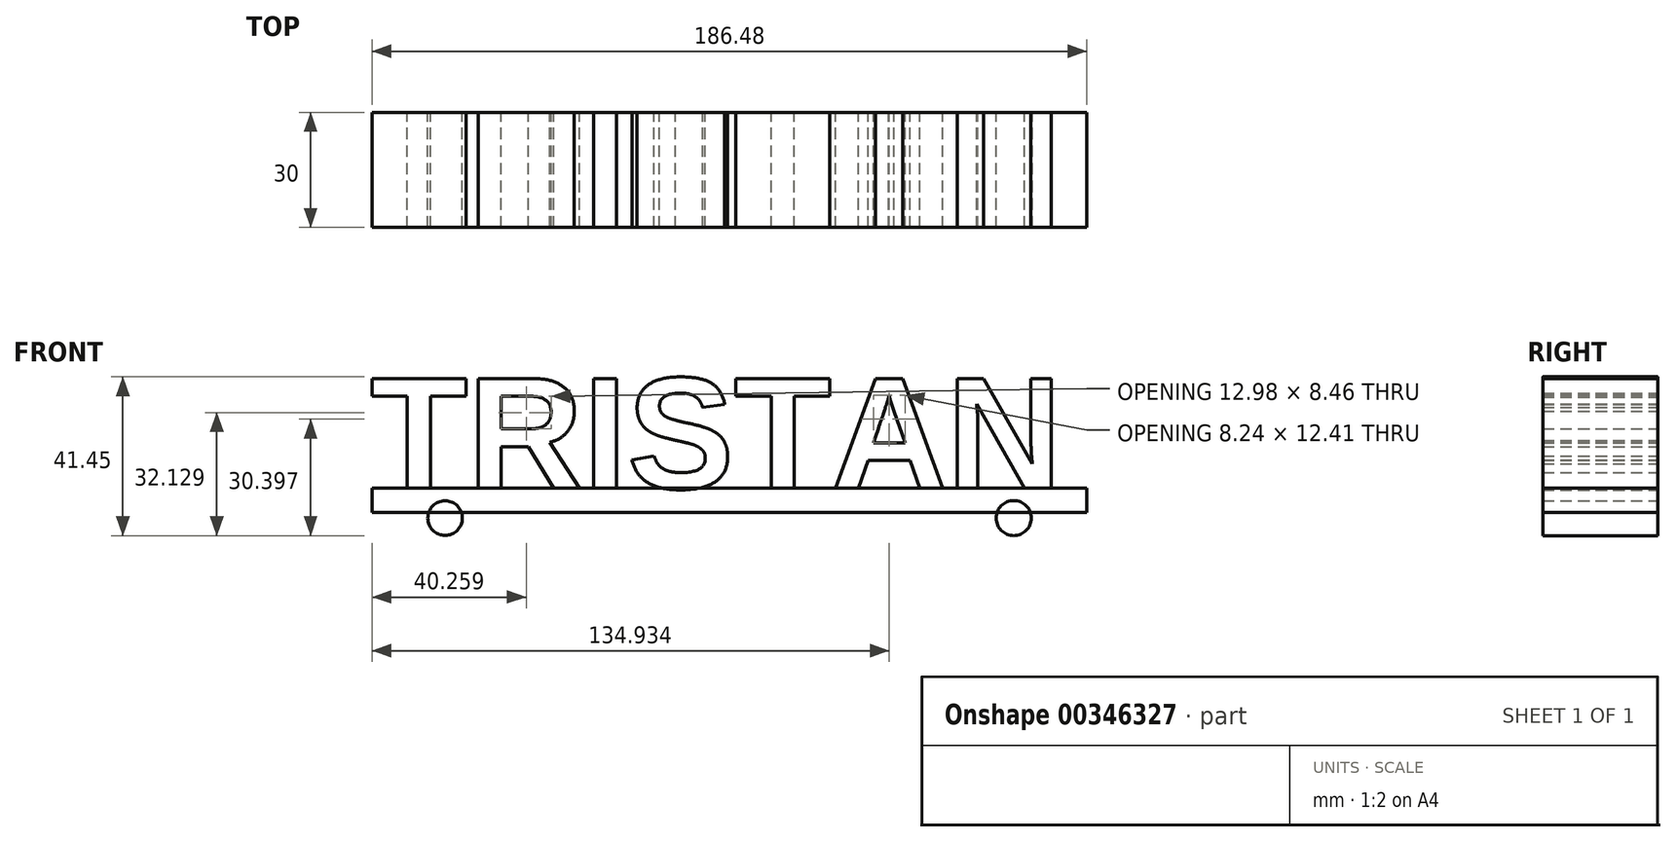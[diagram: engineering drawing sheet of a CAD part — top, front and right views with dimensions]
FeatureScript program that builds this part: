
annotation { "Feature Type Name" : "Feature", "Feature Type Description" : "" }
export const myFeature = defineFeature(function(context is Context, id is Id, definition is map)
    precondition{}
    {
        {
            var Q0;
            Q0=qCreatedBy(makeId("Front.planeOp"),FACE);
            var sketch = newSketch(context, id + "F0", { "sketchPlane" : qUnion([Q0])});
            skText(sketch, "E0", { "text": "TRISTAN", "fontName": "Arimo-Bold.ttf"});
            const initialGuessF0  = {"E0": [-0.08922, -0.01347, 1, 0, 0.03]};
            skSetInitialGuess(sketch, initialGuessF0);
            skSolve(sketch);
        }
        {
            var Q0;
            Q0 = qSketchRegion(id + "F0", true);
            extrude(context, id + "F1", {"entities" : qUnion([Q0]), "depth" : 30 * mm});
        }
        {
            var Q0;
            Q0=qCreatedBy(makeId("Front.planeOp"),FACE);
            var sketch = newSketch(context, id + "F2", { "sketchPlane" : qUnion([Q0])});
            skLineSegment(sketch, "E1.bottom", {"start": v(-88.7, -13.43) * mm, "end": v(97.73, -13.43) * mm});
            skLineSegment(sketch, "E1.top", {"start": v(-88.7, -19.73) * mm, "end": v(97.73, -19.73) * mm});
            skLineSegment(sketch, "E1.left", {"start": v(-88.7, -13.43) * mm, "end": v(-88.7, -19.73) * mm});
            skLineSegment(sketch, "E1.right", {"start": v(97.73, -13.43) * mm, "end": v(97.73, -19.73) * mm});
            skSolve(sketch);
        }
        {
            var Q0;
            Q0=makeQuery(id+"F2.imprint","IMPRINT",FACE,{"disambiguationData":[TD([[makeQuery(id+"F2.imprint","IMPRINT",EDGE,{"derivedFrom":sQuery(id+"F2.wireOp",EDGE,"E1.bottom")}),-1.0]])]});
            extrude(context, id + "F3", {"entities" : qUnion([Q0]), "depth" : 30 * mm});
        }
        {
            var Q0;
            Q0=qCreatedBy(makeId("Front.planeOp"),FACE);
            var sketch = newSketch(context, id + "F4", { "sketchPlane" : qUnion([Q0])});
            skCircle(sketch, "E2", {"center": v(-69.66, -21.24) * mm, "radius": 4.52 * mm});
            skCircle(sketch, "E3", {"center": v(78.68, -21.24) * mm, "radius": 4.58 * mm});
            skSolve(sketch);
        }
        {
            var Q0;
            Q0=makeQuery(id+"F4.imprint","IMPRINT",FACE,{"disambiguationData":[TD([[makeQuery(id+"F4.imprint","IMPRINT",EDGE,{"derivedFrom":sQuery(id+"F4.wireOp",EDGE,"E2")}),1.0]])]});
            var Q1;
            Q1=makeQuery(id+"F4.imprint","IMPRINT",FACE,{"disambiguationData":[TD([[makeQuery(id+"F4.imprint","IMPRINT",EDGE,{"derivedFrom":sQuery(id+"F4.wireOp",EDGE,"E3")}),1.0]])]});
            extrude(context, id + "F5", {"entities" : qUnion([Q0, Q1]), "depth" : 30 * mm});
        }
    });
